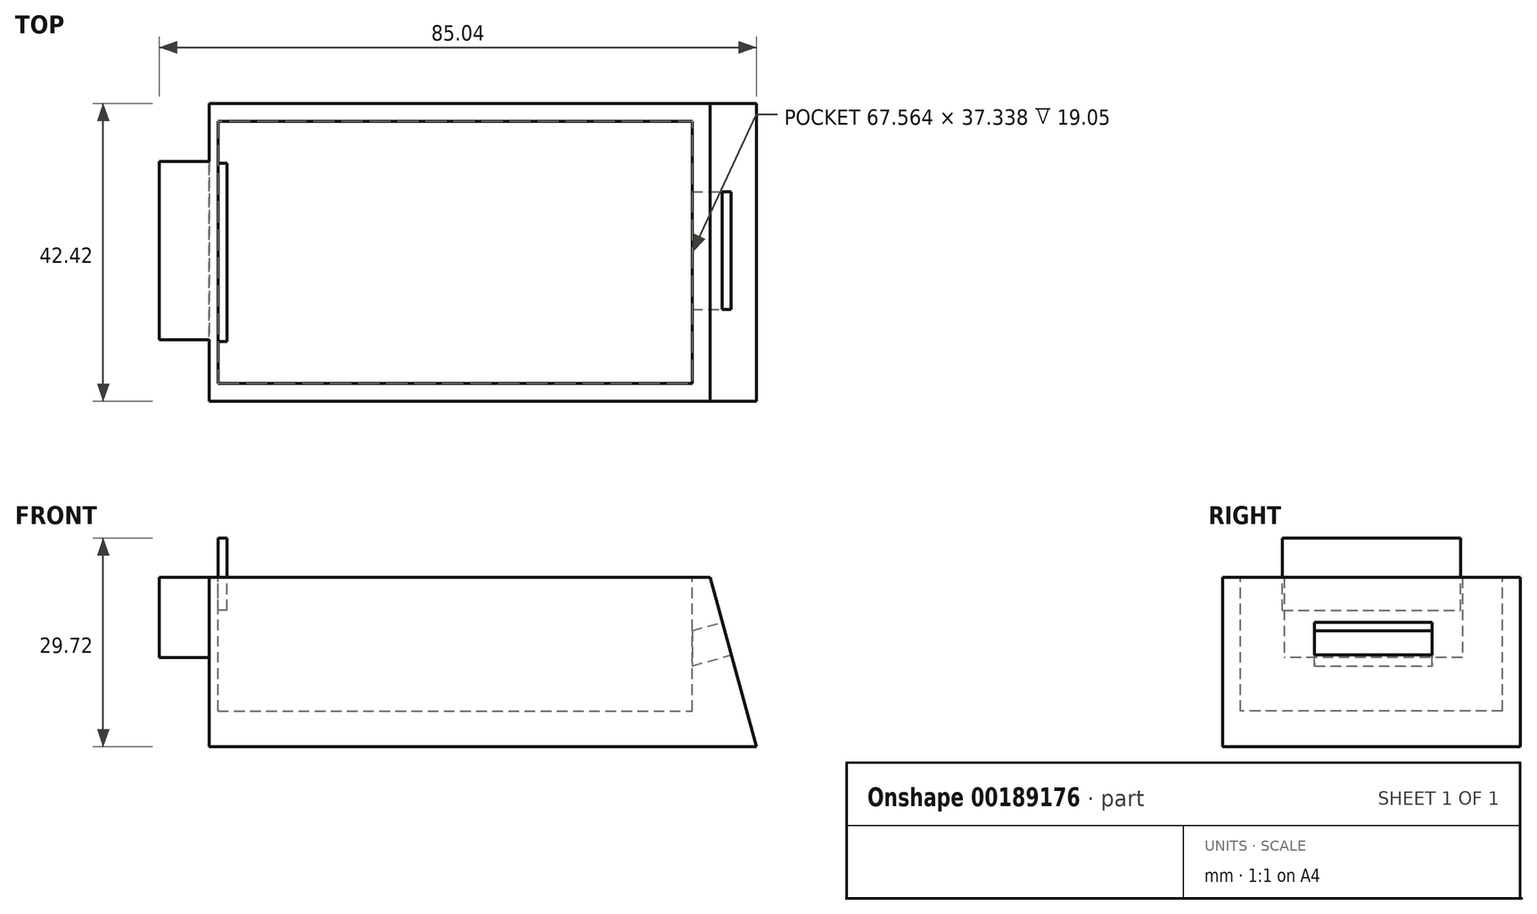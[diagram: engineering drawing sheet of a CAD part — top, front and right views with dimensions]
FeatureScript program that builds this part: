
annotation { "Feature Type Name" : "Feature", "Feature Type Description" : "" }
export const myFeature = defineFeature(function(context is Context, id is Id, definition is map)
    precondition{}
    {
        {
            var Q0;
            Q0=qCreatedBy(makeId("Front.planeOp"),FACE);
            var sketch = newSketch(context, id + "F0", { "sketchPlane" : qUnion([Q0])});
            skLineSegment(sketch, "E0", {"start": v(0, 0) * mm, "end": v(-77.98, 0) * mm});
            skLineSegment(sketch, "E1", {"start": v(-77.98, 24.13) * mm, "end": v(-6.6, 24.13) * mm});
            skLineSegment(sketch, "E2", {"start": v(-77.98, 0) * mm, "end": v(-77.98, 24.13) * mm});
            skLineSegment(sketch, "E3", {"start": v(-6.6, 24.13) * mm, "end": v(0, 0) * mm});
            skSolve(sketch);
        }
        {
            var Q0;
            Q0 = qSketchRegion(id + "F0", true);
            extrude(context, id + "F1", {"entities" : qUnion([Q0]), "endBound" : BoundingType.SYMMETRIC, "depth" : 42.42 * mm});
        }
        {
            var Q0;
            Q0=makeQuery(id+"F1.opExtrude","SWEPT_FACE",FACE,{"disambiguationData":[OSD([sQuery(id+"F0.wireOp",EDGE,"E2")])]});
            var sketch = newSketch(context, id + "F2", { "sketchPlane" : qUnion([Q0])});
            skLineSegment(sketch, "E4.bottom", {"start": v(-12.95, 24.13) * mm, "end": v(12.45, 24.13) * mm});
            skLineSegment(sketch, "E4.top", {"start": v(-12.95, 12.7) * mm, "end": v(12.45, 12.7) * mm});
            skLineSegment(sketch, "E4.left", {"start": v(-12.95, 24.13) * mm, "end": v(-12.95, 12.7) * mm});
            skLineSegment(sketch, "E4.right", {"start": v(12.45, 24.13) * mm, "end": v(12.45, 12.7) * mm});
            skSolve(sketch);
        }
        {
            var Q0;
            Q0 = qSketchRegion(id + "F2", true);
            extrude(context, id + "F3", {"entities" : qUnion([Q0]), "operationType" : NewBodyOperationType.ADD, "depth" : 7.06 * mm});
        }
        {
            var Q0;
            Q0=makeQuery(id+"F1.opExtrude","SWEPT_FACE",FACE,{"disambiguationData":[OSD([sQuery(id+"F0.wireOp",EDGE,"E3")])]});
            var sketch = newSketch(context, id + "F4", { "sketchPlane" : qUnion([Q0])});
            skLineSegment(sketch, "E5.bottom", {"start": v(-8.13, 18.36) * mm, "end": v(8.64, 18.36) * mm});
            skLineSegment(sketch, "E5.top", {"start": v(-8.13, 13.54) * mm, "end": v(8.64, 13.54) * mm});
            skLineSegment(sketch, "E5.left", {"start": v(-8.13, 18.36) * mm, "end": v(-8.13, 13.54) * mm});
            skLineSegment(sketch, "E5.right", {"start": v(8.64, 18.36) * mm, "end": v(8.64, 13.54) * mm});
            skSolve(sketch);
        }
        {
            var Q0;
            Q0 = qSketchRegion(id + "F4", true);
            extrude(context, id + "F5", {"entities" : qUnion([Q0]), "operationType" : NewBodyOperationType.REMOVE, "oppositeDirection" : true, "depth" : 7.37 * mm});
        }
        {
            var Q0;
            Q0=makeQuery(id+"F3.boolean.opBoolean","MERGE",FACE,{"derivedFrom":[makeQuery(id+"F1.opExtrude","SWEPT_FACE",FACE,{"disambiguationData":[OSD([sQuery(id+"F0.wireOp",EDGE,"E1")])]}),makeQuery(id+"F3.opExtrude","SWEPT_FACE",FACE,{"disambiguationData":[OSD([sQuery(id+"F2.wireOp",EDGE,"E4.bottom")])]})]});
            var sketch = newSketch(context, id + "F6", { "sketchPlane" : qUnion([Q0])});
            skPoint(sketch, "E6.firstSnap0", {"position": v(-77.98, 18.67) * mm});
            skLineSegment(sketch, "E6.bottom", {"start": v(-76.7, 18.67) * mm, "end": v(-9.14, 18.67) * mm});
            skLineSegment(sketch, "E6.top", {"start": v(-76.7, -18.67) * mm, "end": v(-9.14, -18.67) * mm});
            skLineSegment(sketch, "E6.left", {"start": v(-76.7, 18.67) * mm, "end": v(-76.7, -18.67) * mm});
            skLineSegment(sketch, "E6.right", {"start": v(-9.14, 18.67) * mm, "end": v(-9.14, -18.67) * mm});
            skSolve(sketch);
        }
        {
            var Q0;
            Q0 = qSketchRegion(id + "F6", true);
            extrude(context, id + "F7", {"entities" : qUnion([Q0]), "operationType" : NewBodyOperationType.REMOVE, "oppositeDirection" : true, "depth" : 19.05 * mm});
        }
        {
            var Q0;
            Q0=makeQuery(id+"F7.boolean.opBoolean","COPY",FACE,{"derivedFrom":makeQuery(id+"F7.opExtrude","SWEPT_FACE",FACE,{"disambiguationData":[OSD([sQuery(id+"F6.wireOp",EDGE,"E6.left")])]})});
            var sketch = newSketch(context, id + "F8", { "sketchPlane" : qUnion([Q0])});
            skLineSegment(sketch, "E7.bottom", {"start": v(-12.7, 19.44) * mm, "end": v(12.7, 19.44) * mm});
            skLineSegment(sketch, "E7.top", {"start": v(-12.7, 29.72) * mm, "end": v(12.7, 29.72) * mm});
            skLineSegment(sketch, "E7.left", {"start": v(-12.7, 19.44) * mm, "end": v(-12.7, 29.72) * mm});
            skLineSegment(sketch, "E7.right", {"start": v(12.7, 19.44) * mm, "end": v(12.7, 29.72) * mm});
            skSolve(sketch);
        }
        {
            var Q0;
            Q0 = qSketchRegion(id + "F8", true);
            extrude(context, id + "F9", {"entities" : qUnion([Q0]), "operationType" : NewBodyOperationType.ADD, "depth" : 1.27 * mm});
        }
    });
